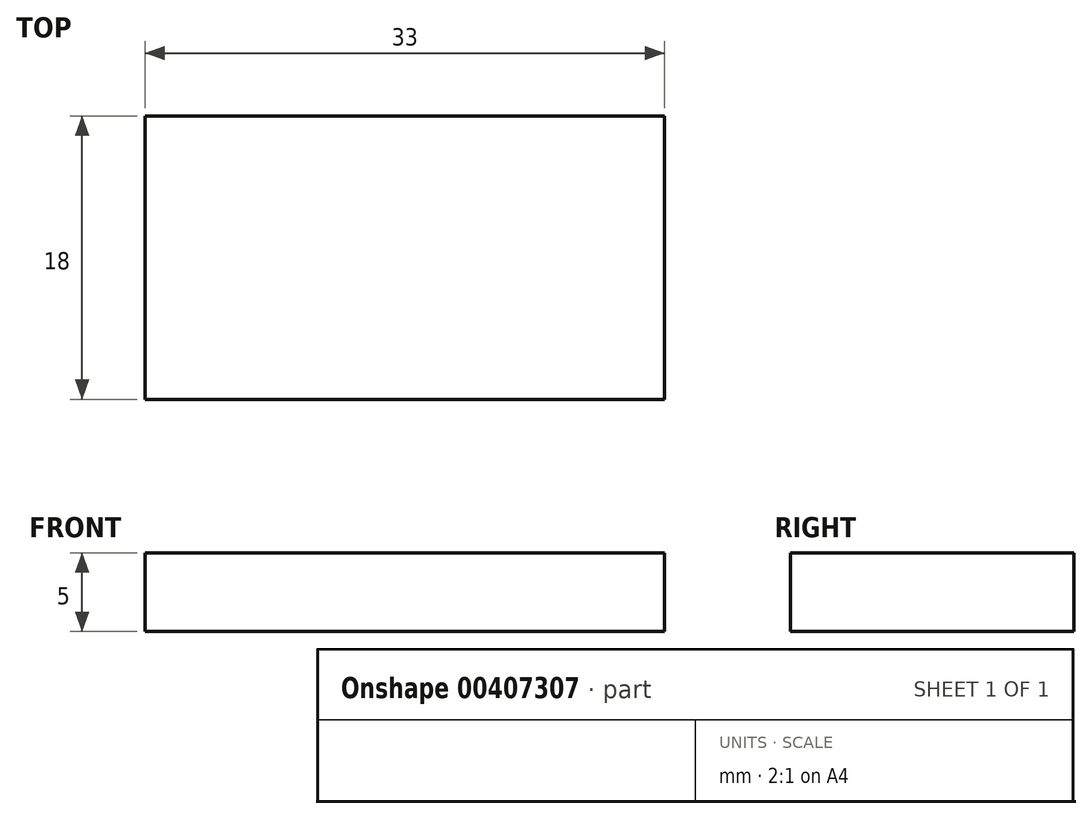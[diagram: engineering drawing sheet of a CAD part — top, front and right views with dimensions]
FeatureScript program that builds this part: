
annotation { "Feature Type Name" : "Feature", "Feature Type Description" : "" }
export const myFeature = defineFeature(function(context is Context, id is Id, definition is map)
    precondition{}
    {
        {
            var Q0;
            Q0=qCreatedBy(makeId("Top.planeOp"),FACE);
            var sketch = newSketch(context, id + "F0", { "sketchPlane" : qUnion([Q0])});
            skLineSegment(sketch, "E0.bottom", {"start": v(0, 0) * mm, "end": v(33, 0) * mm});
            skLineSegment(sketch, "E0.top", {"start": v(0, -18) * mm, "end": v(33, -18) * mm});
            skLineSegment(sketch, "E0.left", {"start": v(0, 0) * mm, "end": v(0, -18) * mm});
            skLineSegment(sketch, "E0.right", {"start": v(33, 0) * mm, "end": v(33, -18) * mm});
            skSolve(sketch);
        }
        {
            var Q0;
            Q0 = qSketchRegion(id + "F0", true);
            extrude(context, id + "F1", {"entities" : qUnion([Q0]), "depth" : 5 * mm});
        }
    });
